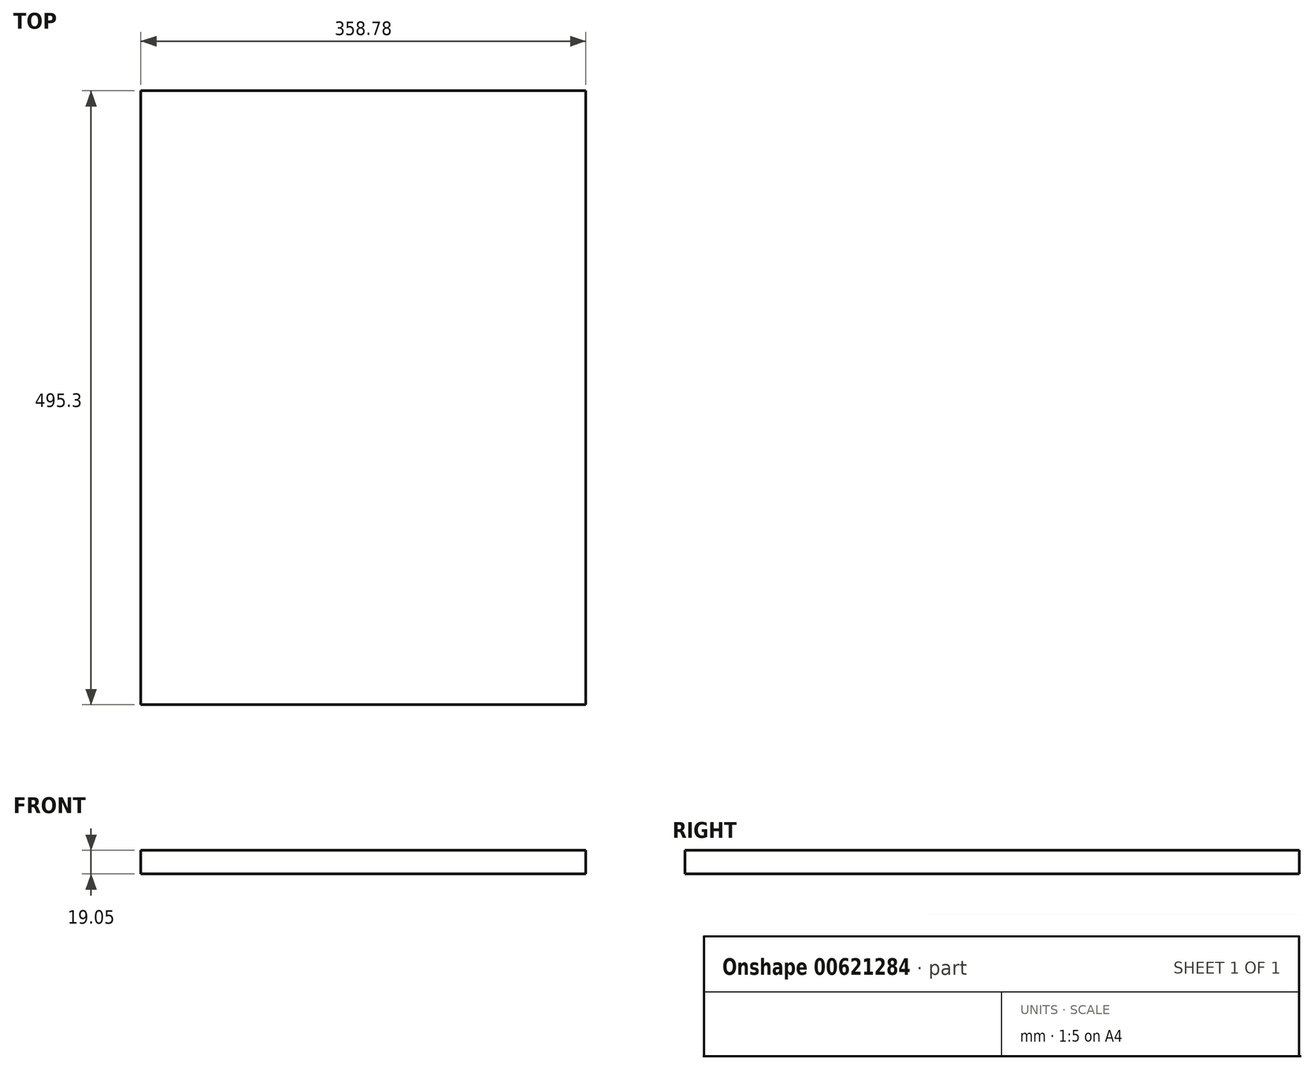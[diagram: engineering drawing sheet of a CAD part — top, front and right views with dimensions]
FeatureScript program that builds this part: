
annotation { "Feature Type Name" : "Feature", "Feature Type Description" : "" }
export const myFeature = defineFeature(function(context is Context, id is Id, definition is map)
    precondition{}
    {
        {
            var Q0;
            Q0=qCreatedBy(makeId("Top.planeOp"),FACE);
            var sketch = newSketch(context, id + "F0", { "sketchPlane" : qUnion([Q0])});
            skLineSegment(sketch, "E0.bottom", {"start": v(179.39, 247.65) * mm, "end": v(-179.39, 247.65) * mm});
            skLineSegment(sketch, "E0.top", {"start": v(179.39, -247.65) * mm, "end": v(-179.39, -247.65) * mm});
            skLineSegment(sketch, "E0.left", {"start": v(179.39, 247.65) * mm, "end": v(179.39, -247.65) * mm});
            skLineSegment(sketch, "E0.right", {"start": v(-179.39, 247.65) * mm, "end": v(-179.39, -247.65) * mm});
            skPoint(sketch, "E0.middle", {"position": v(0, 0) * mm});
            skSolve(sketch);
        }
        {
            var Q0;
            Q0=makeQuery(id+"F0.imprint","IMPRINT",FACE,{"disambiguationData":[TD([[makeQuery(id+"F0.imprint","IMPRINT",EDGE,{"derivedFrom":sQuery(id+"F0.wireOp",EDGE,"E0.bottom")}),1.0]])]});
            extrude(context, id + "F1", {"entities" : qUnion([Q0]), "depth" : 19.05 * mm, "offsetDistance" : 25.4 * mm});
        }
    });
